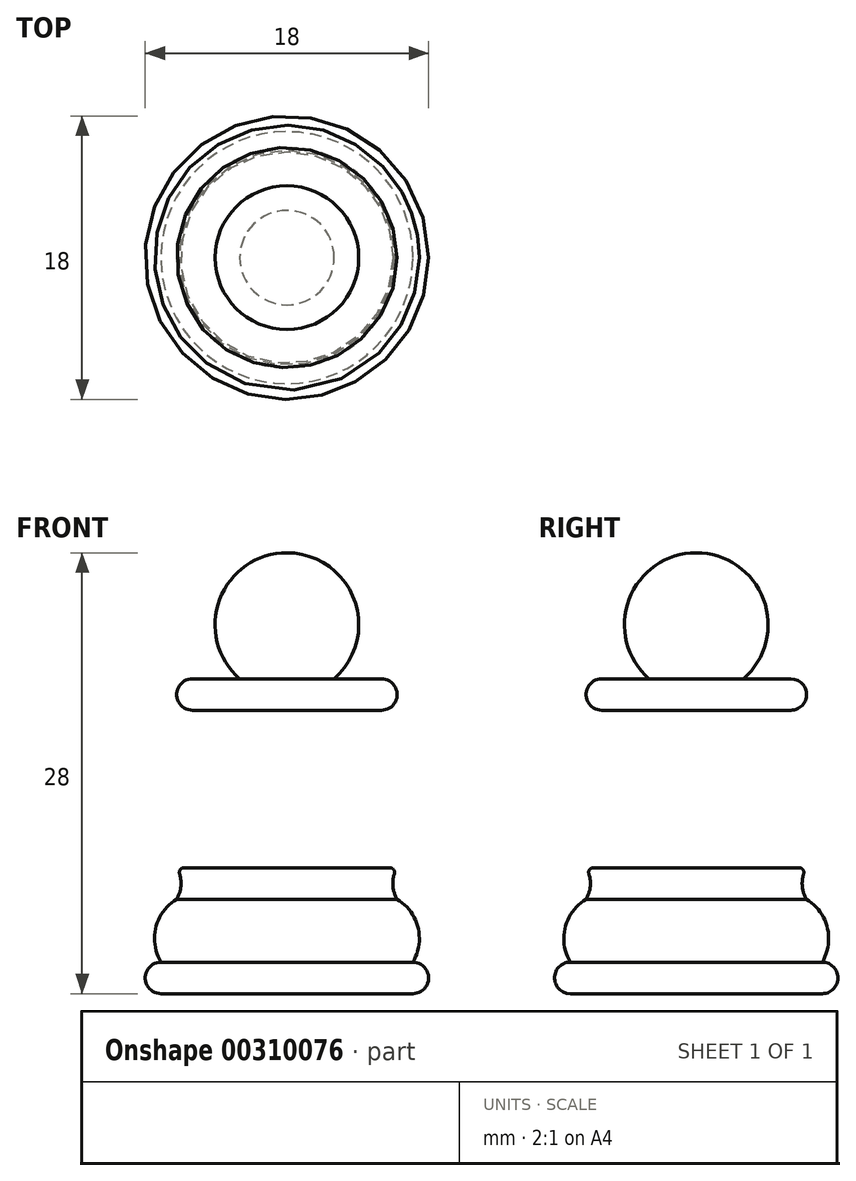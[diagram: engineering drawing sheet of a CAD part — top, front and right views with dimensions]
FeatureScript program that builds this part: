
annotation { "Feature Type Name" : "Feature", "Feature Type Description" : "" }
export const myFeature = defineFeature(function(context is Context, id is Id, definition is map)
    precondition{}
    {
        {
            var Q0;
            Q0=qCreatedBy(makeId("Front.planeOp"),FACE);
            var sketch = newSketch(context, id + "F0", { "sketchPlane" : qUnion([Q0])});
            skLineSegment(sketch, "E0", {"start": v(-33.76, 36.1) * mm, "end": v(-33.76, 6.1) * mm});
            skLineSegment(sketch, "E1", {"start": v(-33.76, 6.1) * mm, "end": v(-33.76, 8.1) * mm});
            skLineSegment(sketch, "E2", {"start": v(-33.76, 8.1) * mm, "end": v(-33.76, 12.1) * mm});
            skLineSegment(sketch, "E3", {"start": v(-33.76, 12.1) * mm, "end": v(-33.76, 14.1) * mm});
            skLineSegment(sketch, "E4", {"start": v(-33.76, 14.1) * mm, "end": v(-43.76, 14.1) * mm});
            skLineSegment(sketch, "E5", {"start": v(-43.76, 14.1) * mm, "end": v(-43.76, 12.1) * mm});
            skLineSegment(sketch, "E6", {"start": v(-33.76, 14.1) * mm, "end": v(-42.76, 14.1) * mm});
            skLineSegment(sketch, "E7", {"start": v(-33.76, 14.1) * mm, "end": v(-33.76, 24.1) * mm});
            skLineSegment(sketch, "E8", {"start": v(-33.76, 24.1) * mm, "end": v(-42.76, 24.1) * mm});
            skLineSegment(sketch, "E9", {"start": v(-36.76, 24.1) * mm, "end": v(-36.76, 6.1) * mm});
            skLineSegment(sketch, "E10", {"start": v(-33.76, 6.1) * mm, "end": v(-36.76, 6.1) * mm});
            skLineSegment(sketch, "E11", {"start": v(-36.76, 26.1) * mm, "end": v(-36.76, 38.26) * mm});
            skLineSegment(sketch, "E12", {"start": v(-36.76, 26.1) * mm, "end": v(-36.76, 24.1) * mm});
            skArc(sketch, "E13", {"start": v(-42.76, 26.1) * mm, "mid": v(-43.76, 25.1) * mm, "end": v(-42.76, 24.1) * mm});
            skLineSegment(sketch, "E14", {"start": v(-36.76, 26.1) * mm, "end": v(-39.76, 26.1) * mm});
            skLineSegment(sketch, "E15", {"start": v(-42.76, 26.1) * mm, "end": v(-39.76, 26.1) * mm});
            skLineSegment(sketch, "E16", {"start": v(-36.76, 26.1) * mm, "end": v(-36.76, 34.1) * mm});
            skLineSegment(sketch, "E17", {"start": v(-36.76, 34.1) * mm, "end": v(-35.53, 34.1) * mm});
            skArc(sketch, "E18", {"start": v(-36.76, 34.1) * mm, "mid": v(-41.03, 31.14) * mm, "end": v(-39.76, 26.1) * mm});
            skLineSegment(sketch, "E19", {"start": v(-36.76, 24.1) * mm, "end": v(-39.76, 24.1) * mm});
            skArc(sketch, "E20", {"start": v(-42.76, 14.1) * mm, "mid": v(-40.38, 18.84) * mm, "end": v(-39.76, 24.1) * mm});
            skLineSegment(sketch, "E21", {"start": v(-33.76, 6.1) * mm, "end": v(-44.76, 6.1) * mm});
            skLineSegment(sketch, "E22", {"start": v(-33.76, 8.1) * mm, "end": v(-44.76, 8.1) * mm});
            skArc(sketch, "E23", {"start": v(-44.76, 8.1) * mm, "mid": v(-45.76, 7.1) * mm, "end": v(-44.76, 6.1) * mm});
            skArc(sketch, "E24", {"start": v(-43.76, 12.1) * mm, "mid": v(-45.08, 10.3) * mm, "end": v(-44.76, 8.1) * mm});
            skArc(sketch, "E25", {"start": v(-43.76, 12.1) * mm, "mid": v(-43.48, 13.1) * mm, "end": v(-43.76, 14.1) * mm});
            skSolve(sketch);
        }
        {
            var Q0;
            Q0=makeQuery(id+"F0.imprint","IMPRINT",FACE,{"disambiguationData":[TD([[makeQuery(id+"F0.imprint","IMPRINT",EDGE,{"derivedFrom":sQuery(id+"F0.wireOp",EDGE,"E14")}),-1.0]])]});
            var Q1;
            Q1=makeQuery(id+"F0.imprint","IMPRINT",FACE,{"disambiguationData":[TD([[makeQuery(id+"F0.imprint","IMPRINT",EDGE,{"derivedFrom":sQuery(id+"F0.wireOp",EDGE,"E12")}),-1.0]])]});
            var Q2;
            {var subQ4=sQuery(id+"F0.wireOp",EDGE,"E19");Q2=makeQuery(id+"F0.imprint","IMPRINT",FACE,{"disambiguationData":[TD([[makeQuery(id+"F0.imprint","IMPRINT",EDGE,{"derivedFrom":subQ4}),1.0]])]});}
            var Q3;
            {var subQ6=sQuery(id+"F0.wireOp",EDGE,"E4");Q3=makeQuery(id+"F0.imprint","IMPRINT",FACE,{"disambiguationData":[TD([[makeQuery(id+"F0.imprint","IMPRINT",EDGE,{"derivedFrom":subQ6}),1.0]])]});}
            var Q4;
            {var subQ5=sQuery(id+"F0.wireOp",EDGE,"E23");Q4=makeQuery(id+"F0.imprint","IMPRINT",FACE,{"disambiguationData":[TD([[makeQuery(id+"F0.imprint","IMPRINT",EDGE,{"derivedFrom":subQ5}),1.0]])]});}
            var Q5;
            Q5=sQuery(id+"F0.wireOp",EDGE,"E9");
            revolve(context, id + "F1", {"entities" : qUnion([Q0, Q1, Q2, Q3, Q4]), "axis" : qUnion([Q5]), "revolveType" : RevolveType.FULL});
        }
        {
            var Q0;
            Q0=makeQuery(id+"F1.opRevolve","SWEPT_EDGE",EDGE,{"disambiguationData":[OSD([sQuery(id+"F0.wireOp",EDGE,"E4"),sQuery(id+"F0.wireOp",EDGE,"E5"),sQuery(id+"F0.wireOp",EDGE,"E25")])]});
            fillet(context, id + "F2", {"entities" : qUnion([Q0]), "radius" : 0.3 * mm, "tangentPropagation" : true, "allowEdgeOverflow" : false});
        }
    });
